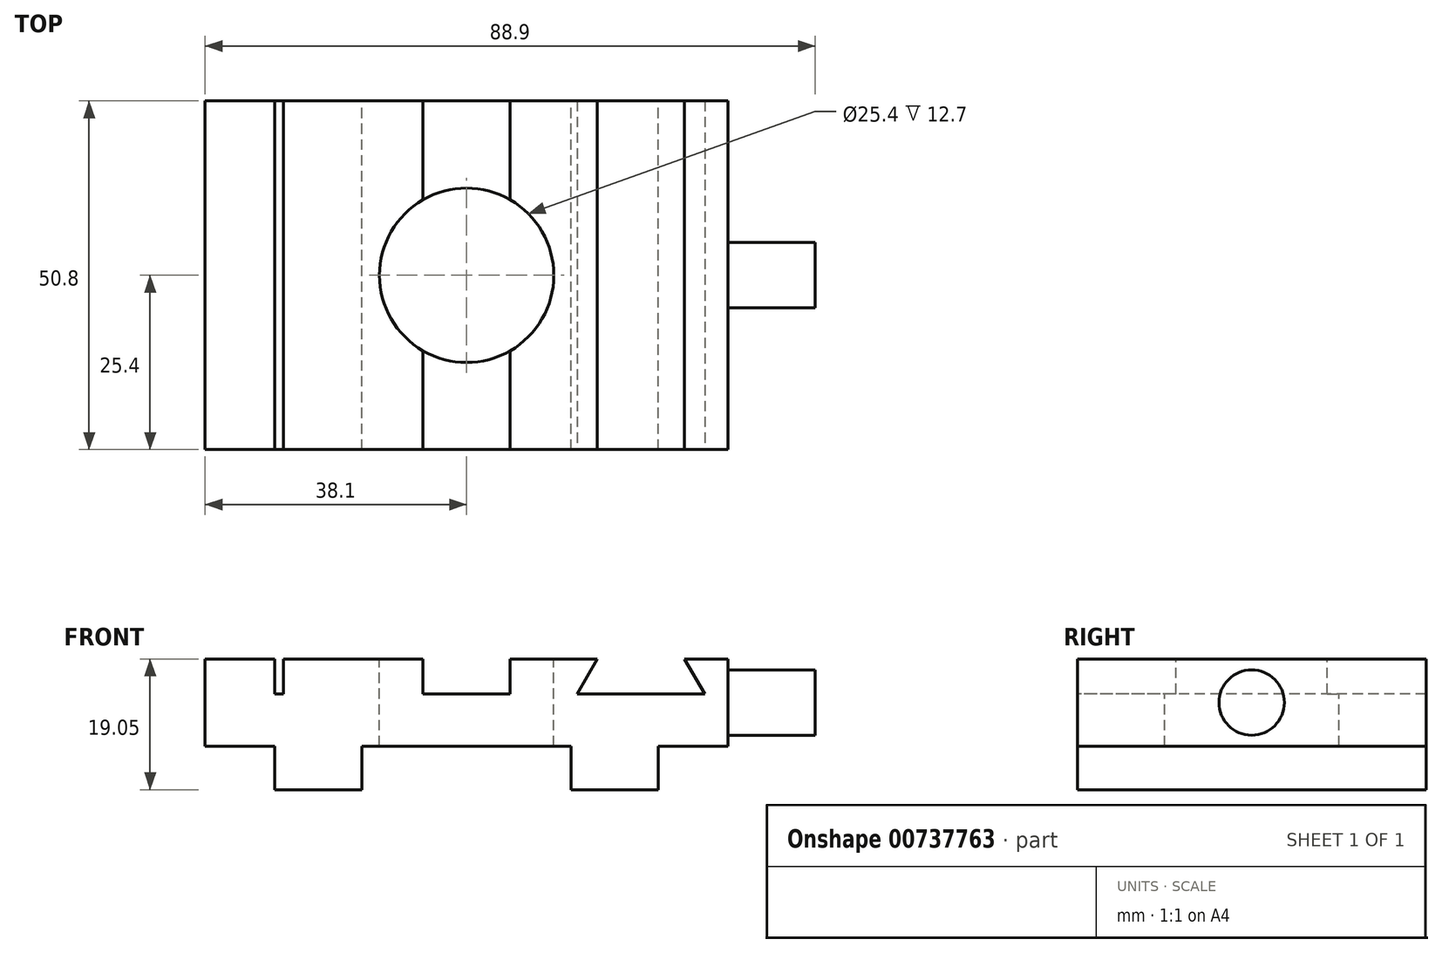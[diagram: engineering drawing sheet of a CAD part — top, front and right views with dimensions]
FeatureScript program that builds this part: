
annotation { "Feature Type Name" : "Feature", "Feature Type Description" : "" }
export const myFeature = defineFeature(function(context is Context, id is Id, definition is map)
    precondition{}
    {
        {
            var Q0;
            Q0=qCreatedBy(makeId("Top.planeOp"),FACE);
            var sketch = newSketch(context, id + "F0", { "sketchPlane" : qUnion([Q0])});
            skLineSegment(sketch, "E0.bottom", {"start": v(38.1, -25.4) * mm, "end": v(-38.1, -25.4) * mm});
            skLineSegment(sketch, "E0.top", {"start": v(38.1, 25.4) * mm, "end": v(-38.1, 25.4) * mm});
            skLineSegment(sketch, "E0.left", {"start": v(38.1, -25.4) * mm, "end": v(38.1, 25.4) * mm});
            skLineSegment(sketch, "E0.right", {"start": v(-38.1, -25.4) * mm, "end": v(-38.1, 25.4) * mm});
            skPoint(sketch, "E0.middle", {"position": v(0, 0) * mm});
            skCircle(sketch, "E1", {"center": v(0, 0) * mm, "radius": 12.7 * mm});
            skSolve(sketch);
        }
        {
            var Q0;
            Q0=makeQuery(id+"F0.imprint","IMPRINT",FACE,{"disambiguationData":[TD([[makeQuery(id+"F0.imprint","IMPRINT",EDGE,{"derivedFrom":sQuery(id+"F0.wireOp",EDGE,"E0.bottom")}),-1.0]])]});
            extrude(context, id + "F1", {"entities" : qUnion([Q0]), "oppositeDirection" : true, "depth" : 12.7 * mm, "offsetDistance" : 25.4 * mm});
        }
        {
            var Q0;
            Q0=makeQuery(id+"F1.opExtrude","CAP_FACE",FACE,{"disambiguationData":[OSD([sQuery(id+"F0.wireOp",EDGE,"E0.bottom"),sQuery(id+"F0.wireOp",EDGE,"E0.top"),sQuery(id+"F0.wireOp",EDGE,"E0.left"),sQuery(id+"F0.wireOp",EDGE,"E0.right"),sQuery(id+"F0.wireOp",EDGE,"E1")])],"isStart":true});
            var sketch = newSketch(context, id + "F2", { "sketchPlane" : qUnion([Q0])});
            skLineSegment(sketch, "E2.bottom", {"start": v(-27.94, 25.4) * mm, "end": v(-26.67, 25.4) * mm});
            skLineSegment(sketch, "E2.top", {"start": v(-27.94, -25.4) * mm, "end": v(-26.67, -25.4) * mm});
            skLineSegment(sketch, "E2.left", {"start": v(-27.94, 25.4) * mm, "end": v(-27.94, -25.4) * mm});
            skLineSegment(sketch, "E2.right", {"start": v(-26.67, 25.4) * mm, "end": v(-26.67, -25.4) * mm});
            skLineSegment(sketch, "E3", {"start": v(-6.35, 25.4) * mm, "end": v(-6.35, -25.4) * mm});
            skLineSegment(sketch, "E4", {"start": v(6.35, -25.4) * mm, "end": v(6.35, 25.4) * mm});
            skLineSegment(sketch, "E5", {"start": v(6.35, 25.4) * mm, "end": v(-6.35, 25.4) * mm});
            skPoint(sketch, "E6", {"position": v(0, 0) * mm});
            skLineSegment(sketch, "E7", {"start": v(0, 25.4) * mm, "end": v(0, -25.4) * mm, "construction": true});
            skPoint(sketch, "E7.endSnap0", {"position": v(0, -25.4) * mm});
            skSolve(sketch);
        }
        {
            var Q0;
            Q0=makeQuery(id+"F2.imprint","IMPRINT",FACE,{"disambiguationData":[TD([[makeQuery(id+"F2.imprint","IMPRINT",EDGE,{"derivedFrom":sQuery(id+"F2.wireOp",EDGE,"E2.bottom")}),1.0]])]});
            var Q1;
            {var subQ0=sQuery(id+"F2.wireOp",EDGE,"E3");var subQ1=makeQuery(id+"F1.opExtrude","CAP_EDGE",EDGE,{"disambiguationData":[OSD([sQuery(id+"F0.wireOp",EDGE,"E0.bottom")])],"isStart":true});var subQ2=makeQuery(id+"F2.imprint","INTERSECT",VERTEX,{"derivedFrom":[subQ1,subQ0]});Q1=makeQuery(id+"F2.imprint","IMPRINT",FACE,{"disambiguationData":[TD([[makeQuery(id+"F2.imprint","IMPRINT",EDGE,{"disambiguationData":[TD([[subQ2,1.0]])],"derivedFrom":subQ0}),1.0]])]});}
            var Q2;
            {var subQ0=sQuery(id+"F2.wireOp",EDGE,"E5");Q2=makeQuery(id+"F2.imprint","IMPRINT",FACE,{"disambiguationData":[TD([[makeQuery(id+"F2.imprint","IMPRINT",EDGE,{"derivedFrom":subQ0}),1.0]])]});}
            extrude(context, id + "F3", {"entities" : qUnion([Q0, Q1, Q2]), "operationType" : NewBodyOperationType.REMOVE, "oppositeDirection" : true, "depth" : 5.08 * mm, "offsetDistance" : 25.4 * mm});
        }
        {
            var Q0;
            Q0=makeQuery(id+"F1.opExtrude","SWEPT_FACE",FACE,{"disambiguationData":[OSD([sQuery(id+"F0.wireOp",EDGE,"E0.bottom")])]});
            var sketch = newSketch(context, id + "F4", { "sketchPlane" : qUnion([Q0])});
            skLineSegment(sketch, "E8", {"start": v(19.05, 0) * mm, "end": v(16.12, -5.08) * mm});
            skLineSegment(sketch, "E9", {"start": v(16.12, -5.08) * mm, "end": v(34.68, -5.08) * mm});
            skLineSegment(sketch, "E10", {"start": v(34.68, -5.08) * mm, "end": v(31.75, 0) * mm});
            skLineSegment(sketch, "E11", {"start": v(31.75, 0) * mm, "end": v(19.05, 0) * mm});
            skLineSegment(sketch, "E12", {"start": v(25.4, -5.08) * mm, "end": v(25.4, 0) * mm, "construction": true});
            skSolve(sketch);
        }
        {
            var Q0;
            Q0=makeQuery(id+"F4.imprint","IMPRINT",FACE,{"disambiguationData":[TD([[makeQuery(id+"F4.imprint","IMPRINT",EDGE,{"derivedFrom":sQuery(id+"F4.wireOp",EDGE,"E8")}),1.0]])]});
            extrude(context, id + "F5", {"entities" : qUnion([Q0]), "operationType" : NewBodyOperationType.REMOVE, "endBound" : BoundingType.THROUGH_ALL, "oppositeDirection" : true, "depth" : 25.4 * mm, "offsetDistance" : 25.4 * mm});
        }
        {
            var Q0;
            Q0=makeQuery(id+"F1.opExtrude","SWEPT_FACE",FACE,{"disambiguationData":[OSD([sQuery(id+"F0.wireOp",EDGE,"E0.left")])]});
            var sketch = newSketch(context, id + "F6", { "sketchPlane" : qUnion([Q0])});
            skCircle(sketch, "E13", {"center": v(0, -6.35) * mm, "radius": 4.76 * mm});
            skPoint(sketch, "E13.centerSnap0", {"position": v(-25.4, -6.35) * mm});
            skPoint(sketch, "E13.centerSnap1", {"position": v(0, 0) * mm});
            skSolve(sketch);
        }
        {
            var Q0;
            Q0=makeQuery(id+"F6.imprint","IMPRINT",FACE,{"disambiguationData":[TD([[makeQuery(id+"F6.imprint","IMPRINT",EDGE,{"derivedFrom":sQuery(id+"F6.wireOp",EDGE,"E13")}),1.0]])]});
            extrude(context, id + "F7", {"entities" : qUnion([Q0]), "operationType" : NewBodyOperationType.ADD, "depth" : 12.7 * mm, "offsetDistance" : 25.4 * mm});
        }
        {
            var Q0;
            Q0=makeQuery(id+"F1.opExtrude","CAP_FACE",FACE,{"disambiguationData":[OSD([sQuery(id+"F0.wireOp",EDGE,"E0.bottom"),sQuery(id+"F0.wireOp",EDGE,"E0.top"),sQuery(id+"F0.wireOp",EDGE,"E0.left"),sQuery(id+"F0.wireOp",EDGE,"E0.right"),sQuery(id+"F0.wireOp",EDGE,"E1")])],"isStart":false});
            var sketch = newSketch(context, id + "F8", { "sketchPlane" : qUnion([Q0])});
            skLineSegment(sketch, "E14.bottom", {"start": v(-27.94, 25.4) * mm, "end": v(-15.24, 25.4) * mm});
            skLineSegment(sketch, "E14.top", {"start": v(-27.94, -25.4) * mm, "end": v(-15.24, -25.4) * mm});
            skLineSegment(sketch, "E14.left", {"start": v(-27.94, 25.4) * mm, "end": v(-27.94, -25.4) * mm});
            skLineSegment(sketch, "E14.right", {"start": v(-15.24, 25.4) * mm, "end": v(-15.24, -25.4) * mm});
            skLineSegment(sketch, "E15.bottom", {"start": v(15.24, 25.4) * mm, "end": v(27.94, 25.4) * mm});
            skLineSegment(sketch, "E15.top", {"start": v(15.24, -25.4) * mm, "end": v(27.94, -25.4) * mm});
            skLineSegment(sketch, "E15.left", {"start": v(15.24, 25.4) * mm, "end": v(15.24, -25.4) * mm});
            skLineSegment(sketch, "E15.right", {"start": v(27.94, 25.4) * mm, "end": v(27.94, -25.4) * mm});
            skSolve(sketch);
        }
        {
            var Q0;
            Q0=makeQuery(id+"F8.imprint","IMPRINT",FACE,{"disambiguationData":[TD([[makeQuery(id+"F8.imprint","IMPRINT",EDGE,{"derivedFrom":sQuery(id+"F8.wireOp",EDGE,"E14.bottom")}),1.0]])]});
            var Q1;
            Q1=makeQuery(id+"F8.imprint","IMPRINT",FACE,{"disambiguationData":[TD([[makeQuery(id+"F8.imprint","IMPRINT",EDGE,{"derivedFrom":sQuery(id+"F8.wireOp",EDGE,"E15.bottom")}),1.0]])]});
            extrude(context, id + "F9", {"entities" : qUnion([Q0, Q1]), "operationType" : NewBodyOperationType.ADD, "depth" : 6.35 * mm, "offsetDistance" : 25.4 * mm});
        }
    });
